# Revit family: Standard-Quattro-Nostalgia-3D
name_source: partatom
category: Furniture
units: mm (PartAtom-declared; Revit-internal decimal feet)

## family parameters
Always vertical = Yes
Classification Number = 23.40.50.11.11.11
Cut with Voids When Loaded = No
Enable Cutting in Views = No
Render Appearance Source = Family Geometry
Room Calculation Point = No
Shared = No
Work Plane-Based = No

## types (1)
- Standard-Quattro-Nostalgia-3D
    Accent Color = <By Category>
    Armrest Base Finish = <By Category>
    Armrest Finish = <By Category>
    Assembly Code = E2010500
    BIM Version = v3.1
    BIM Version Available (Earliest) = 2017
    CSI MasterFormat = 12 61 00
    Default Elevation = 0"
    Description = Quattro Nostalgic End Standard
    Manufacturer = Hussey Seating Company
    Product Page URL = http://www.husseyseating.com
    Series = Quattro Collection - Nostalgia Series
    Stanchion Finish = <By Category>
    URL = http://www.husseyseating.com

## geometry (parser evidence)
native form markers: Sweep x2
no freeform markers — native parametric forms only
